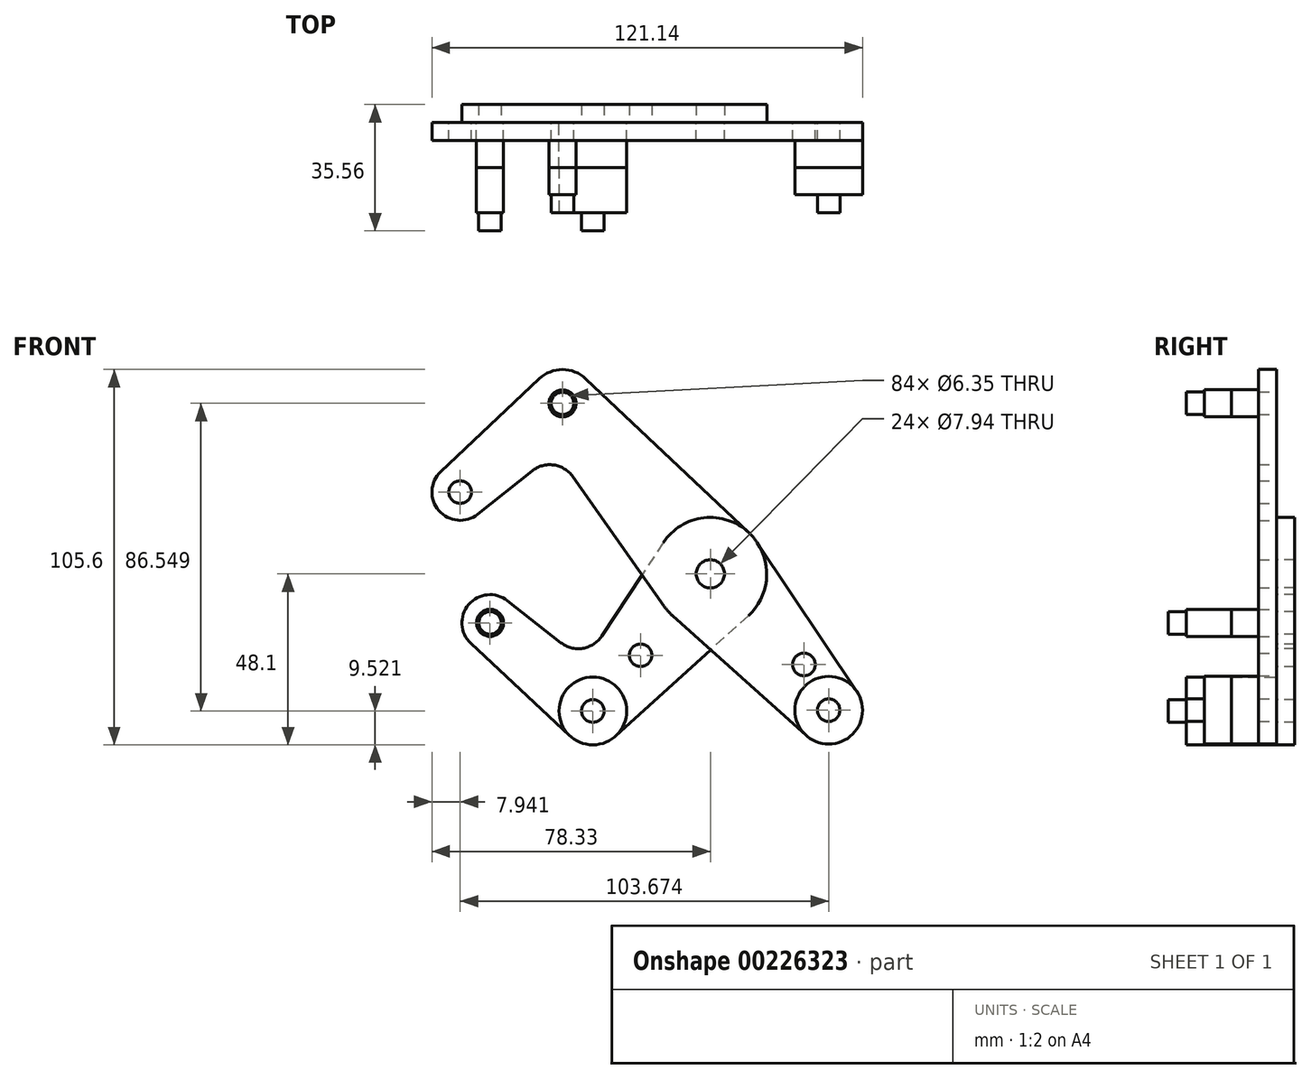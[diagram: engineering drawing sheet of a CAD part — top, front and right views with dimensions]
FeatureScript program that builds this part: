
annotation { "Feature Type Name" : "Feature", "Feature Type Description" : "" }
export const myFeature = defineFeature(function(context is Context, id is Id, definition is map)
    precondition{}
    {
        {
            var Q0;
            Q0=qCreatedBy(makeId("Front.planeOp"),FACE);
            var sketch = newSketch(context, id + "F0", { "sketchPlane" : qUnion([Q0])});
            skLineSegment(sketch, "E0", {"start": v(-41.6, 47.97) * mm, "end": v(41.6, -47.97) * mm, "construction": true});
            skCircle(sketch, "E1", {"center": v(0, 0) * mm, "radius": 3.18 * mm});
            skCircle(sketch, "E2", {"center": v(33.29, -38.38) * mm, "radius": 3.18 * mm});
            skCircle(sketch, "E3", {"center": v(-41.6, 47.97) * mm, "radius": 3.18 * mm});
            skCircle(sketch, "E4", {"center": v(-70.39, 23) * mm, "radius": 3.18 * mm});
            skLineSegment(sketch, "E5", {"start": v(-41.6, 47.97) * mm, "end": v(-70.39, 23) * mm, "construction": true});
            skCircle(sketch, "E6", {"center": v(33.29, -38.38) * mm, "radius": 9.53 * mm});
            skCircle(sketch, "E7", {"center": v(-70.39, 23) * mm, "radius": 7.94 * mm});
            skCircle(sketch, "E8", {"center": v(-41.6, 47.97) * mm, "radius": 9.53 * mm});
            skLineSegment(sketch, "E9", {"start": v(-75.83, 28.78) * mm, "end": v(-48.14, 54.9) * mm});
            skLineSegment(sketch, "E10", {"start": v(-65.44, 16.8) * mm, "end": v(-50.15, 28.98) * mm});
            skCircle(sketch, "E11", {"center": v(0, 0) * mm, "radius": 15.88 * mm});
            skLineSegment(sketch, "E12", {"start": v(-35.07, 54.9) * mm, "end": v(10.9, 11.55) * mm});
            skLineSegment(sketch, "E13", {"start": v(-38.72, 27.35) * mm, "end": v(-12.97, -9.15) * mm});
            skLineSegment(sketch, "E14", {"start": v(-10.6, -11.82) * mm, "end": v(26.93, -45.47) * mm});
            skLineSegment(sketch, "E15", {"start": v(13.2, 8.82) * mm, "end": v(41.2, -33.08) * mm});
            skArc(sketch, "E16.filletArc", {"start": v(-38.72, 27.35) * mm, "mid": v(-44.08, 30.63) * mm, "end": v(-50.15, 28.98) * mm});
            skLineSegment(sketch, "E17", {"start": v(0, 0) * mm, "end": v(-33.05, -38.58) * mm, "construction": true});
            skLineSegment(sketch, "E18", {"start": v(-33.05, -38.58) * mm, "end": v(-61.98, -13.8) * mm, "construction": true});
            skCircle(sketch, "E19", {"center": v(-61.98, -13.8) * mm, "radius": 3.18 * mm});
            skCircle(sketch, "E20", {"center": v(-33.05, -38.58) * mm, "radius": 3.18 * mm});
            skCircle(sketch, "E21", {"center": v(-61.98, -13.8) * mm, "radius": 7.94 * mm});
            skCircle(sketch, "E22", {"center": v(-33.05, -38.58) * mm, "radius": 9.53 * mm});
            skLineSegment(sketch, "E23", {"start": v(-57.08, -7.55) * mm, "end": v(-42.08, -19.35) * mm});
            skLineSegment(sketch, "E24", {"start": v(-67.4, -19.6) * mm, "end": v(-39.54, -45.55) * mm});
            skLineSegment(sketch, "E25", {"start": v(-13.25, 8.74) * mm, "end": v(-30.55, -17.48) * mm});
            skLineSegment(sketch, "E26", {"start": v(10.67, -11.75) * mm, "end": v(-26.65, -45.63) * mm});
            skArc(sketch, "E27.filletArc", {"start": v(-42.08, -19.35) * mm, "mid": v(-35.9, -20.95) * mm, "end": v(-30.55, -17.48) * mm});
            skCircle(sketch, "E28", {"center": v(-19.62, -22.9) * mm, "radius": 3.18 * mm});
            skCircle(sketch, "E29", {"center": v(26.32, -25.5) * mm, "radius": 3.18 * mm});
            skLineSegment(sketch, "E30", {"start": v(26.32, -25.5) * mm, "end": v(23.92, -27.58) * mm, "construction": true});
            skCircle(sketch, "E31", {"center": v(0, 0) * mm, "radius": 3.97 * mm});
            skSolve(sketch);
        }
        {
            var Q0;
            Q0=qCreatedBy(makeId("Front.planeOp"),FACE);
            cPlane(context, id + "F1", {"entities" : qUnion([Q0]), "cplaneType" : CPlaneType.OFFSET, "offset" : 12.7 * mm, "width" : 254 * mm, "height" : 254 * mm});
        }
        {
            var Q0;
            Q0=makeQuery(id+"F0.imprint","IMPRINT",FACE,{"disambiguationData":[TD([[makeQuery(id+"F0.imprint","IMPRINT",EDGE,{"derivedFrom":sQuery(id+"F0.wireOp",EDGE,"E2")}),-1.0]])]});
            var Q1;
            {var subQ0=sQuery(id+"F0.wireOp",EDGE,"E15");Q1=makeQuery(id+"F0.imprint","IMPRINT",FACE,{"disambiguationData":[TD([[makeQuery(id+"F0.imprint","IMPRINT",EDGE,{"derivedFrom":subQ0}),-1.0]])]});}
            var Q2;
            {var subQ0=sQuery(id+"F0.wireOp",EDGE,"E14");var subQ1=sQuery(id+"F0.wireOp",EDGE,"E11");var subQ2=makeQuery(id+"F0.imprint","INTERSECT",VERTEX,{"derivedFrom":[subQ1,subQ0]});Q2=makeQuery(id+"F0.imprint","IMPRINT",FACE,{"disambiguationData":[TD([[makeQuery(id+"F0.imprint","IMPRINT",EDGE,{"disambiguationData":[TD([[subQ2,-1.0]])],"derivedFrom":subQ1}),-1.0]])]});}
            var Q3;
            Q3=makeQuery(id+"F0.imprint","IMPRINT",FACE,{"disambiguationData":[TD([[makeQuery(id+"F0.imprint","IMPRINT",EDGE,{"derivedFrom":sQuery(id+"F0.wireOp",EDGE,"E31")}),-1.0]])]});
            var Q4;
            {var subQ0=sQuery(id+"F0.wireOp",EDGE,"E13");var subQ1=sQuery(id+"F0.wireOp",EDGE,"E11");var subQ2=makeQuery(id+"F0.imprint","INTERSECT",VERTEX,{"derivedFrom":[subQ1,subQ0]});Q4=makeQuery(id+"F0.imprint","IMPRINT",FACE,{"disambiguationData":[TD([[makeQuery(id+"F0.imprint","IMPRINT",EDGE,{"disambiguationData":[TD([[subQ2,1.0]])],"derivedFrom":subQ1}),-1.0]])]});}
            var Q5;
            {var subQ1=sQuery(id+"F0.wireOp",EDGE,"E9");Q5=makeQuery(id+"F0.imprint","IMPRINT",FACE,{"disambiguationData":[TD([[makeQuery(id+"F0.imprint","IMPRINT",EDGE,{"derivedFrom":subQ1}),-1.0]])]});}
            var Q6;
            Q6=makeQuery(id+"F0.imprint","IMPRINT",FACE,{"disambiguationData":[TD([[makeQuery(id+"F0.imprint","IMPRINT",EDGE,{"derivedFrom":sQuery(id+"F0.wireOp",EDGE,"E3")}),-1.0]])]});
            var Q7;
            Q7=makeQuery(id+"F0.imprint","IMPRINT",FACE,{"disambiguationData":[TD([[makeQuery(id+"F0.imprint","IMPRINT",EDGE,{"derivedFrom":sQuery(id+"F0.wireOp",EDGE,"E4")}),-1.0]])]});
            extrude(context, id + "F2", {"entities" : qUnion([Q0, Q1, Q2, Q3, Q4, Q5, Q6, Q7]), "depth" : 5.08 * mm});
        }
        {
            var Q0;
            Q0=makeQuery(id+"F0.imprint","IMPRINT",FACE,{"disambiguationData":[TD([[makeQuery(id+"F0.imprint","IMPRINT",EDGE,{"derivedFrom":sQuery(id+"F0.wireOp",EDGE,"E19")}),-1.0]])]});
            var Q1;
            {var subQ10=sQuery(id+"F0.wireOp",EDGE,"E23");Q1=makeQuery(id+"F0.imprint","IMPRINT",FACE,{"disambiguationData":[TD([[makeQuery(id+"F0.imprint","IMPRINT",EDGE,{"derivedFrom":subQ10}),-1.0]])]});}
            var Q2;
            Q2=makeQuery(id+"F0.imprint","IMPRINT",FACE,{"disambiguationData":[TD([[makeQuery(id+"F0.imprint","IMPRINT",EDGE,{"derivedFrom":sQuery(id+"F0.wireOp",EDGE,"E20")}),-1.0]])]});
            var Q3;
            Q3=makeQuery(id+"F0.imprint","IMPRINT",FACE,{"disambiguationData":[TD([[makeQuery(id+"F0.imprint","IMPRINT",EDGE,{"derivedFrom":sQuery(id+"F0.wireOp",EDGE,"E31")}),-1.0]])]});
            var Q4;
            {var subQ0=sQuery(id+"F0.wireOp",EDGE,"E14");var subQ1=sQuery(id+"F0.wireOp",EDGE,"E11");var subQ2=makeQuery(id+"F0.imprint","INTERSECT",VERTEX,{"derivedFrom":[subQ1,subQ0]});Q4=makeQuery(id+"F0.imprint","IMPRINT",FACE,{"disambiguationData":[TD([[makeQuery(id+"F0.imprint","IMPRINT",EDGE,{"disambiguationData":[TD([[subQ2,-1.0]])],"derivedFrom":subQ1}),-1.0]])]});}
            var Q5;
            {var subQ0=sQuery(id+"F0.wireOp",EDGE,"E13");var subQ1=sQuery(id+"F0.wireOp",EDGE,"E11");var subQ2=makeQuery(id+"F0.imprint","INTERSECT",VERTEX,{"derivedFrom":[subQ1,subQ0]});Q5=makeQuery(id+"F0.imprint","IMPRINT",FACE,{"disambiguationData":[TD([[makeQuery(id+"F0.imprint","IMPRINT",EDGE,{"disambiguationData":[TD([[subQ2,1.0]])],"derivedFrom":subQ1}),-1.0]])]});}
            extrude(context, id + "F3", {"entities" : qUnion([Q0, Q1, Q2, Q3, Q4, Q5]), "oppositeDirection" : true, "depth" : 5.08 * mm});
        }
        {
            var Q0;
            Q0=makeQuery(id+"F2.opExtrude","CAP_FACE",FACE,{"disambiguationData":[OSD([sQuery(id+"F0.wireOp",EDGE,"E2"),sQuery(id+"F0.wireOp",EDGE,"E3"),sQuery(id+"F0.wireOp",EDGE,"E4"),sQuery(id+"F0.wireOp",EDGE,"E6"),sQuery(id+"F0.wireOp",EDGE,"E7"),sQuery(id+"F0.wireOp",EDGE,"E8"),sQuery(id+"F0.wireOp",EDGE,"E9"),sQuery(id+"F0.wireOp",EDGE,"E10"),sQuery(id+"F0.wireOp",EDGE,"E11"),sQuery(id+"F0.wireOp",EDGE,"E12"),sQuery(id+"F0.wireOp",EDGE,"E13"),sQuery(id+"F0.wireOp",EDGE,"E14"),sQuery(id+"F0.wireOp",EDGE,"E15"),sQuery(id+"F0.wireOp",EDGE,"E16.filletArc"),sQuery(id+"F0.wireOp",EDGE,"E29"),sQuery(id+"F0.wireOp",EDGE,"E31")])],"isStart":true});
            var sketch = newSketch(context, id + "F4", { "sketchPlane" : qUnion([Q0])});
            skCircle(sketch, "E32.0", {"center": v(-33.29, -38.38) * mm, "radius": 9.53 * mm});
            skCircle(sketch, "E33", {"center": v(41.6, 47.97) * mm, "radius": 3.81 * mm});
            skSolve(sketch);
        }
        {
            var Q0;
            Q0=makeQuery(id+"F3.opExtrude","CAP_FACE",FACE,{"disambiguationData":[OSD([sQuery(id+"F0.wireOp",EDGE,"E11"),sQuery(id+"F0.wireOp",EDGE,"E19"),sQuery(id+"F0.wireOp",EDGE,"E20"),sQuery(id+"F0.wireOp",EDGE,"E21"),sQuery(id+"F0.wireOp",EDGE,"E22"),sQuery(id+"F0.wireOp",EDGE,"E23"),sQuery(id+"F0.wireOp",EDGE,"E24"),sQuery(id+"F0.wireOp",EDGE,"E25"),sQuery(id+"F0.wireOp",EDGE,"E26"),sQuery(id+"F0.wireOp",EDGE,"E27.filletArc"),sQuery(id+"F0.wireOp",EDGE,"E28"),sQuery(id+"F0.wireOp",EDGE,"E31")])],"isStart":false});
            var sketch = newSketch(context, id + "F5", { "sketchPlane" : qUnion([Q0])});
            skCircle(sketch, "E34", {"center": v(61.98, -13.8) * mm, "radius": 3.81 * mm});
            skCircle(sketch, "E35.0", {"center": v(33.05, -38.58) * mm, "radius": 9.53 * mm});
            skSolve(sketch);
        }
        {
            var Q0;
            Q0 = qSketchRegion(id + "F4", true);
            var Q1;
            Q1 = qSketchRegion(id + "F5", true);
            var Q2;
            Q2=qCreatedBy(id+"F1.planeOp",FACE);
            extrude(context, id + "F6", {"entities" : qUnion([Q0, Q1]), "endBound" : BoundingType.UP_TO_SURFACE, "oppositeDirection" : true, "endBoundEntityFace" : qUnion([Q2]), "depth" : 25.4 * mm});
        }
        {
            var Q0;
            Q0=makeQuery(id+"F2.opExtrude","SWEPT_BODY",BODY,{"disambiguationData":[OSD([sQuery(id+"F0.wireOp",EDGE,"E2"),sQuery(id+"F0.wireOp",EDGE,"E3"),sQuery(id+"F0.wireOp",EDGE,"E4"),sQuery(id+"F0.wireOp",EDGE,"E6"),sQuery(id+"F0.wireOp",EDGE,"E7"),sQuery(id+"F0.wireOp",EDGE,"E8"),sQuery(id+"F0.wireOp",EDGE,"E9"),sQuery(id+"F0.wireOp",EDGE,"E10"),sQuery(id+"F0.wireOp",EDGE,"E11"),sQuery(id+"F0.wireOp",EDGE,"E12"),sQuery(id+"F0.wireOp",EDGE,"E13"),sQuery(id+"F0.wireOp",EDGE,"E14"),sQuery(id+"F0.wireOp",EDGE,"E15"),sQuery(id+"F0.wireOp",EDGE,"E16.filletArc"),sQuery(id+"F0.wireOp",EDGE,"E29"),sQuery(id+"F0.wireOp",EDGE,"E31")])]});
            var Q1;
            Q1=makeQuery(id+"F3.opExtrude","SWEPT_BODY",BODY,{"disambiguationData":[OSD([sQuery(id+"F0.wireOp",EDGE,"E11"),sQuery(id+"F0.wireOp",EDGE,"E19"),sQuery(id+"F0.wireOp",EDGE,"E20"),sQuery(id+"F0.wireOp",EDGE,"E21"),sQuery(id+"F0.wireOp",EDGE,"E22"),sQuery(id+"F0.wireOp",EDGE,"E23"),sQuery(id+"F0.wireOp",EDGE,"E24"),sQuery(id+"F0.wireOp",EDGE,"E25"),sQuery(id+"F0.wireOp",EDGE,"E26"),sQuery(id+"F0.wireOp",EDGE,"E27.filletArc"),sQuery(id+"F0.wireOp",EDGE,"E28"),sQuery(id+"F0.wireOp",EDGE,"E31")])]});
            var Q2;
            Q2=makeQuery(id+"F6.opExtrude","SWEPT_BODY",BODY,{"disambiguationData":[OSD([sQuery(id+"F4.wireOp",EDGE,"E32.0")])]});
            var Q3;
            Q3=makeQuery(id+"F6.opExtrude","SWEPT_BODY",BODY,{"disambiguationData":[OSD([sQuery(id+"F4.wireOp",EDGE,"E33")])]});
            var Q4;
            Q4=makeQuery(id+"F6.opExtrude","SWEPT_BODY",BODY,{"disambiguationData":[OSD([sQuery(id+"F5.wireOp",EDGE,"E34")])]});
            var Q5;
            Q5=makeQuery(id+"F6.opExtrude","SWEPT_BODY",BODY,{"disambiguationData":[OSD([sQuery(id+"F5.wireOp",EDGE,"E35.0")])]});
            booleanBodies(context, id + "F7", {"operationType" : BooleanOperationType.SUBTRACTION, "tools" : qUnion([Q0, Q1]), "targets" : qUnion([Q2, Q3, Q4, Q5]), "keepTools" : true});
        }
        {
            var Q0;
            Q0=makeQuery(id+"F6.opExtrude","SWEPT_BODY",BODY,{"disambiguationData":[OSD([sQuery(id+"F4.wireOp",EDGE,"E33")])]});
            var Q1;
            Q1=makeQuery(id+"F6.opExtrude","SWEPT_BODY",BODY,{"disambiguationData":[OSD([sQuery(id+"F5.wireOp",EDGE,"E34")])]});
            var Q2;
            Q2=makeQuery(id+"F6.opExtrude","SWEPT_BODY",BODY,{"disambiguationData":[OSD([sQuery(id+"F5.wireOp",EDGE,"E35.0")])]});
            var Q3;
            Q3=makeQuery(id+"F6.opExtrude","SWEPT_BODY",BODY,{"disambiguationData":[OSD([sQuery(id+"F4.wireOp",EDGE,"E32.0")])]});
            var Q4;
            Q4=qCreatedBy(id+"F1.planeOp",FACE);
            mirror(context, id + "F8", {"entities" : qUnion([Q0, Q1, Q2, Q3]), "mirrorPlane" : qUnion([Q4])});
        }
    });
